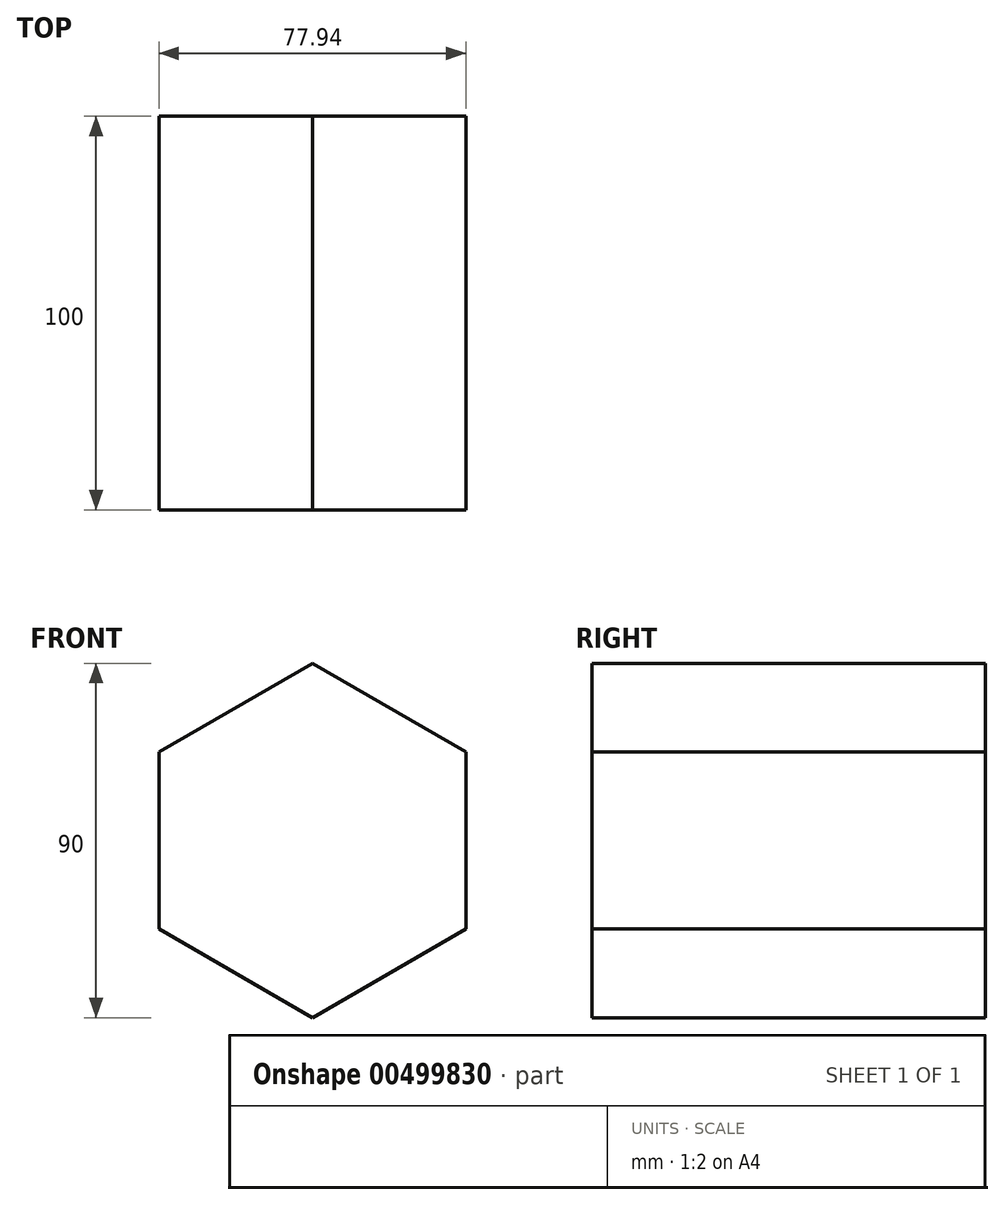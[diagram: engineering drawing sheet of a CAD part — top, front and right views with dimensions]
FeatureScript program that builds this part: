
annotation { "Feature Type Name" : "Feature", "Feature Type Description" : "" }
export const myFeature = defineFeature(function(context is Context, id is Id, definition is map)
    precondition{}
    {
        {
            var Q0;
            Q0=qCreatedBy(makeId("Front.planeOp"),FACE);
            var sketch = newSketch(context, id + "F0", { "sketchPlane" : qUnion([Q0])});
            skCircle(sketch, "E0.cCircle", {"center": v(0, 0) * mm, "radius": 38.97 * mm, "construction": true});
            skLineSegment(sketch, "E0.0", {"start": v(0, 45) * mm, "end": v(38.97, 22.5) * mm});
            skLineSegment(sketch, "E0.1", {"start": v(38.97, 22.5) * mm, "end": v(38.97, -22.5) * mm});
            skLineSegment(sketch, "E0.2", {"start": v(38.97, -22.5) * mm, "end": v(0, -45) * mm});
            skLineSegment(sketch, "E0.3", {"start": v(0, -45) * mm, "end": v(-38.97, -22.5) * mm});
            skLineSegment(sketch, "E0.4", {"start": v(-38.97, -22.5) * mm, "end": v(-38.97, 22.5) * mm});
            skLineSegment(sketch, "E0.5", {"start": v(-38.97, 22.5) * mm, "end": v(0, 45) * mm});
            skPoint(sketch, "E0.0.midPoint", {"position": v(19.49, 33.75) * mm});
            skSolve(sketch);
        }
        {
            var Q0;
            Q0 = qSketchRegion(id + "F0", true);
            extrude(context, id + "F1", {"entities" : qUnion([Q0]), "depth" : 100 * mm, "symmetric" : true});
        }
    });
